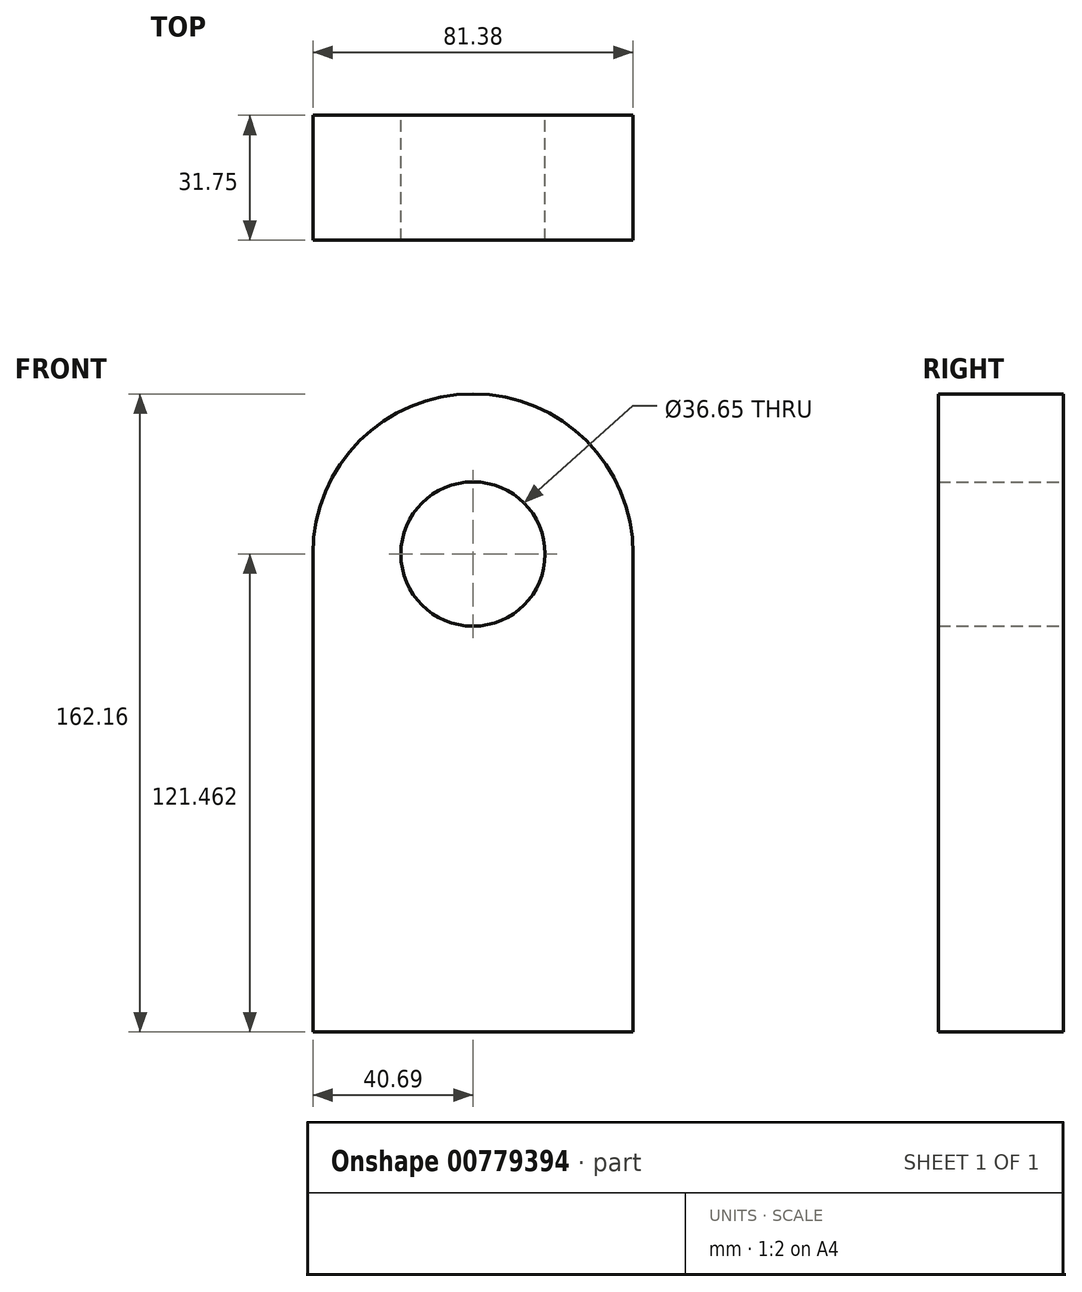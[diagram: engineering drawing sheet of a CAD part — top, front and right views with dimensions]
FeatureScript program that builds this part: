
annotation { "Feature Type Name" : "Feature", "Feature Type Description" : "" }
export const myFeature = defineFeature(function(context is Context, id is Id, definition is map)
    precondition{}
    {
        {
            var Q0;
            Q0=qCreatedBy(makeId("Front.planeOp"),FACE);
            var sketch = newSketch(context, id + "F0", { "sketchPlane" : qUnion([Q0])});
            skLineSegment(sketch, "E0.top", {"start": v(40.7, -60.73) * mm, "end": v(-40.7, -60.73) * mm});
            skLineSegment(sketch, "E0.left", {"start": v(40.7, 60.73) * mm, "end": v(40.7, -60.73) * mm});
            skLineSegment(sketch, "E0.right", {"start": v(-40.7, 60.73) * mm, "end": v(-40.7, -60.73) * mm});
            skPoint(sketch, "E0.middle", {"position": v(0, 0) * mm});
            skArc(sketch, "E1", {"start": v(40.7, 60.73) * mm, "mid": v(0, 101.43) * mm, "end": v(-40.7, 60.73) * mm});
            skCircle(sketch, "E2", {"center": v(0, 60.73) * mm, "radius": 18.33 * mm});
            skSolve(sketch);
        }
        {
            var Q0;
            Q0=makeQuery(id+"F0.imprint","IMPRINT",FACE,{"disambiguationData":[TD([[makeQuery(id+"F0.imprint","IMPRINT",EDGE,{"derivedFrom":sQuery(id+"F0.wireOp",EDGE,"E0.top")}),-1.0]])]});
            extrude(context, id + "F1", {"entities" : qUnion([Q0]), "depth" : 31.75 * mm, "offsetDistance" : 25.4 * mm});
        }
    });
